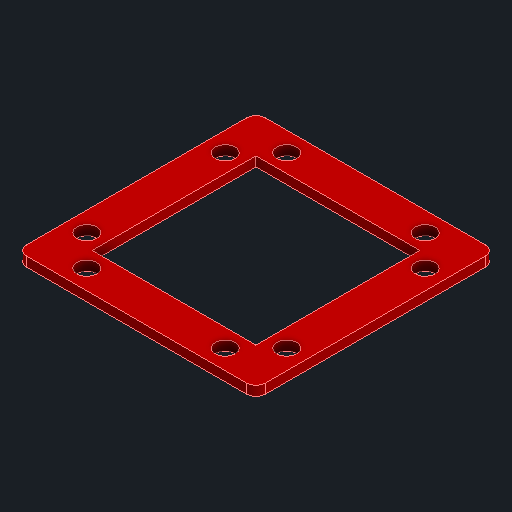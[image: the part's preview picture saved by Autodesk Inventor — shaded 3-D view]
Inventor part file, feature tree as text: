
AUTODESK INVENTOR PART (.ipt)
format: ipt  version: 2023.4 (Build 274418000, 418)  size: 285,184 bytes
history: native  units: mm
features: reference x9, extrude x3, other x3, sketch x2, fillet x1, projected_geometry x1
ambient origin geometry x8: Origin, YZ Plane, XZ Plane, XY Plane, X Axis, Y Axis, Z Axis, Center Point
bodies: Solid1 (feature_tree)
feature tree (19):
  extrude  "Extrusion1"  Depth=2.0mm
  sketch  "Sketch2"  dims[d3=10.0mm d4=45.0deg d5=135.0deg d6=1.0mm d7=1.5mm d8=1.0mm d9=0.075mm d10=40.0mm d12=360.0deg d14=2.0mm d15=0.0mm d16=10.0mm d17=0.0mm d18=0.25mm]
  extrude  "Extrusion2"  TaperAngle=45.0deg  [1 undecoded]
  extrude  "Extrusion3"  TaperAngle=135.0deg  [1 undecoded]
  fillet  "Fillet1"  Radius=1.0mm
  sketch  "Sketch1"  dims[d0=2.0mm d1=0.0mm d2=20.0mm]
  reference  "Reference1"
  reference  "Reference2"
  reference  "Reference3"
  reference  "Reference4"
  reference  "Reference5"
  reference  "Reference6"
  reference  "Reference7"
  reference  "Reference8"
  reference  "Reference9"
  projected_geometry  "Projected Loop1"
  other  "<path>\Projects\Project Protocube\Protocube\CAD, STL, OBJ Files\1 CAD\Cube 1x1 V5.iam"
  other  "Cube 1x1 V5.iam"
  other  "Cube 1x1 Top V5:1"
note: 2 required parameter values undecoded (feature->parameter linkage not recoverable at this tier; creation-order binding heuristic only, values carry confidence <= 0.55)
note: 1 file-system path scrubbed to <path> (originals preserved in map.json)
